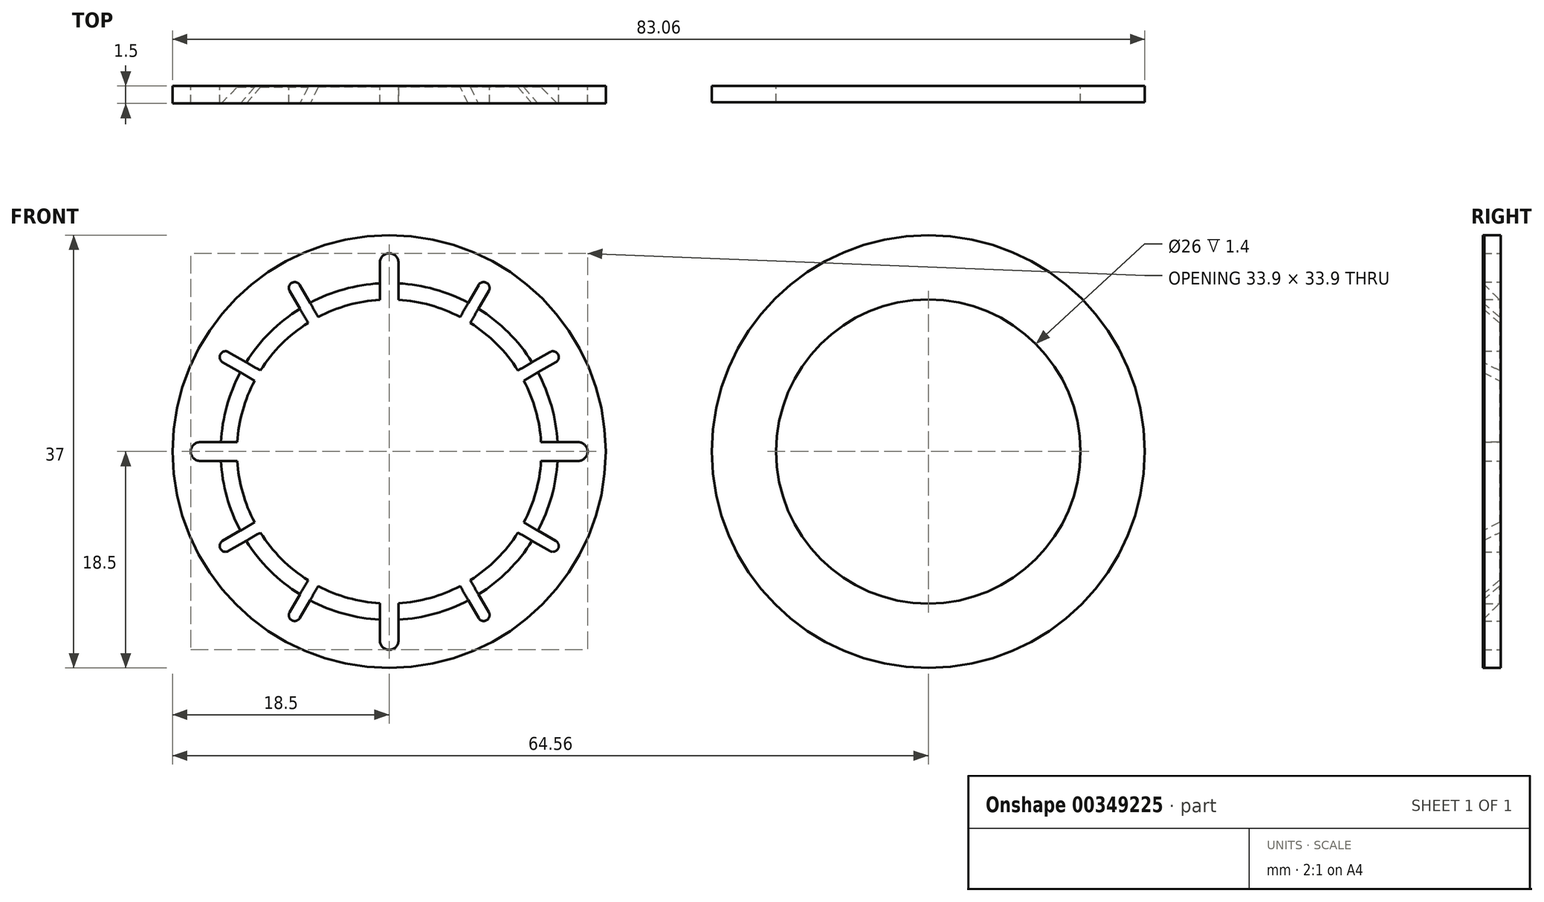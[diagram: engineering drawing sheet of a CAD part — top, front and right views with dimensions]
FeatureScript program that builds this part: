
annotation { "Feature Type Name" : "Feature", "Feature Type Description" : "" }
export const myFeature = defineFeature(function(context is Context, id is Id, definition is map)
    precondition{}
    {
        {
            var Q0;
            Q0=qCreatedBy(makeId("Front.planeOp"),FACE);
            var sketch = newSketch(context, id + "F0", { "sketchPlane" : qUnion([Q0])});
            skCircle(sketch, "E0", {"center": v(0, 0) * mm, "radius": 18.5 * mm});
            skCircle(sketch, "E1", {"center": v(0, 0) * mm, "radius": 13 * mm});
            skCircle(sketch, "E2", {"center": v(-16.15, 0) * mm, "radius": 0.5 * mm});
            skLineSegment(sketch, "E3", {"start": v(-16.15, 0.5) * mm, "end": v(-13, 0.5) * mm});
            skLineSegment(sketch, "E4.MirrorCS", {"start": v(-16.15, -0.5) * mm, "end": v(-13, -0.5) * mm});
            skCircle(sketch, "E5.1.0", {"center": v(-13.99, -8.07) * mm, "radius": 0.5 * mm});
            skLineSegment(sketch, "E5.1.1", {"start": v(-13.74, -8.5) * mm, "end": v(-11, -6.93) * mm});
            skLineSegment(sketch, "E5.1.2", {"start": v(-14.24, -7.64) * mm, "end": v(-11.5, -6.06) * mm});
            skCircle(sketch, "E5.2.0", {"center": v(-8.08, -13.99) * mm, "radius": 0.5 * mm});
            skLineSegment(sketch, "E5.2.1", {"start": v(-7.64, -14.24) * mm, "end": v(-6.06, -11.5) * mm});
            skLineSegment(sketch, "E5.2.2", {"start": v(-8.5, -13.74) * mm, "end": v(-6.93, -11) * mm});
            skCircle(sketch, "E6.1.3.0", {"center": v(0, -16.15) * mm, "radius": 0.5 * mm});
            skLineSegment(sketch, "E6.2.3.0", {"start": v(0.5, -16.15) * mm, "end": v(0.5, -13) * mm});
            skLineSegment(sketch, "E6.5.3.0", {"start": v(-0.5, -16.15) * mm, "end": v(-0.5, -13) * mm});
            skCircle(sketch, "E6.1.4.0", {"center": v(8.07, -13.99) * mm, "radius": 0.5 * mm});
            skLineSegment(sketch, "E6.2.4.0", {"start": v(8.5, -13.74) * mm, "end": v(6.93, -11) * mm});
            skLineSegment(sketch, "E6.5.4.0", {"start": v(7.64, -14.24) * mm, "end": v(6.06, -11.5) * mm});
            skCircle(sketch, "E6.1.5.0", {"center": v(13.99, -8.07) * mm, "radius": 0.5 * mm});
            skLineSegment(sketch, "E6.2.5.0", {"start": v(14.24, -7.64) * mm, "end": v(11.5, -6.06) * mm});
            skLineSegment(sketch, "E6.5.5.0", {"start": v(13.74, -8.5) * mm, "end": v(11, -6.93) * mm});
            skCircle(sketch, "E6.1.6.0", {"center": v(16.15, 0) * mm, "radius": 0.5 * mm});
            skLineSegment(sketch, "E6.2.6.0", {"start": v(16.15, 0.5) * mm, "end": v(13, 0.5) * mm});
            skLineSegment(sketch, "E6.5.6.0", {"start": v(16.15, -0.5) * mm, "end": v(13, -0.5) * mm});
            skCircle(sketch, "E6.1.7.0", {"center": v(13.99, 8.07) * mm, "radius": 0.5 * mm});
            skLineSegment(sketch, "E6.2.7.0", {"start": v(13.74, 8.5) * mm, "end": v(11, 6.93) * mm});
            skLineSegment(sketch, "E6.5.7.0", {"start": v(14.24, 7.64) * mm, "end": v(11.5, 6.06) * mm});
            skCircle(sketch, "E6.1.8.0", {"center": v(8.08, 13.99) * mm, "radius": 0.5 * mm});
            skLineSegment(sketch, "E6.2.8.0", {"start": v(7.64, 14.24) * mm, "end": v(6.06, 11.5) * mm});
            skLineSegment(sketch, "E6.5.8.0", {"start": v(8.5, 13.74) * mm, "end": v(6.93, 11) * mm});
            skCircle(sketch, "E6.1.9.0", {"center": v(0, 16.15) * mm, "radius": 0.5 * mm});
            skLineSegment(sketch, "E6.2.9.0", {"start": v(-0.5, 16.15) * mm, "end": v(-0.5, 13) * mm});
            skLineSegment(sketch, "E6.5.9.0", {"start": v(0.5, 16.15) * mm, "end": v(0.5, 13) * mm});
            skCircle(sketch, "E6.1.10.0", {"center": v(-8.08, 13.99) * mm, "radius": 0.5 * mm});
            skLineSegment(sketch, "E6.2.10.0", {"start": v(-8.5, 13.74) * mm, "end": v(-6.93, 11) * mm});
            skLineSegment(sketch, "E6.5.10.0", {"start": v(-7.64, 14.24) * mm, "end": v(-6.06, 11.5) * mm});
            skCircle(sketch, "E6.1.11.0", {"center": v(-13.99, 8.08) * mm, "radius": 0.5 * mm});
            skLineSegment(sketch, "E6.2.11.0", {"start": v(-14.24, 7.64) * mm, "end": v(-11.5, 6.06) * mm});
            skLineSegment(sketch, "E6.5.11.0", {"start": v(-13.74, 8.5) * mm, "end": v(-11, 6.93) * mm});
            skCircle(sketch, "E7", {"center": v(-16.15, 0) * mm, "radius": 0.8 * mm});
            skLineSegment(sketch, "E8", {"start": v(-16.15, 0.8) * mm, "end": v(-12.98, 0.8) * mm});
            skLineSegment(sketch, "E9.MirrorCS", {"start": v(-16.15, -0.8) * mm, "end": v(-12.98, -0.8) * mm});
            skCircle(sketch, "E10.1.0", {"center": v(0, -16.15) * mm, "radius": 0.8 * mm});
            skLineSegment(sketch, "E10.1.1", {"start": v(-0.8, -16.15) * mm, "end": v(-0.8, -12.98) * mm});
            skLineSegment(sketch, "E10.1.2", {"start": v(0.8, -16.15) * mm, "end": v(0.8, -12.98) * mm});
            skCircle(sketch, "E10.2.0", {"center": v(16.15, 0) * mm, "radius": 0.8 * mm});
            skLineSegment(sketch, "E10.2.1", {"start": v(16.15, -0.8) * mm, "end": v(12.98, -0.8) * mm});
            skLineSegment(sketch, "E10.2.2", {"start": v(16.15, 0.8) * mm, "end": v(12.98, 0.8) * mm});
            skCircle(sketch, "E11.1.3.0", {"center": v(0, 16.15) * mm, "radius": 0.8 * mm});
            skLineSegment(sketch, "E11.2.3.0", {"start": v(0.8, 16.15) * mm, "end": v(0.8, 12.98) * mm});
            skLineSegment(sketch, "E11.5.3.0", {"start": v(-0.8, 16.15) * mm, "end": v(-0.8, 12.98) * mm});
            skCircle(sketch, "E12", {"center": v(46.06, 0) * mm, "radius": 18.5 * mm});
            skCircle(sketch, "E13", {"center": v(46.06, 0) * mm, "radius": 13 * mm});
            skSolve(sketch);
        }
        {
            var Q0;
            {var subQ11=sQuery(id+"F0.wireOp",EDGE,"E6.2.10.0");Q0=makeQuery(id+"F0.imprint","IMPRINT",FACE,{"disambiguationData":[TD([[makeQuery(id+"F0.imprint","IMPRINT",EDGE,{"derivedFrom":subQ11}),-1.0]])]});}
            var Q1;
            {var subQ6=sQuery(id+"F0.wireOp",EDGE,"E5.1.1");Q1=makeQuery(id+"F0.imprint","IMPRINT",FACE,{"disambiguationData":[TD([[makeQuery(id+"F0.imprint","IMPRINT",EDGE,{"derivedFrom":subQ6}),-1.0]])]});}
            extrude(context, id + "F1", {"entities" : qUnion([Q0, Q1]), "offsetDistance" : 25 * mm, "depth" : 1.5 * mm});
        }
        {
            var Q0;
            {var subQ0=sQuery(id+"F0.wireOp",EDGE,"E1");Q0=makeQuery(id+"F1.opExtrude","CAP_EDGE",EDGE,{"disambiguationData":[OSD([subQ0]),TDD([makeQuery(id+"F0.imprint","IMPRINT",EDGE,{"disambiguationData":[TD([[makeQuery(id+"F0.imprint","INTERSECT",VERTEX,{"derivedFrom":[subQ0,sQuery(id+"F0.wireOp",EDGE,"E6.2.11.0")]}),-1.0]])],"derivedFrom":subQ0})])],"isStart":false});}
            var Q1;
            {var subQ0=sQuery(id+"F0.wireOp",EDGE,"E1");Q1=makeQuery(id+"F1.opExtrude","CAP_EDGE",EDGE,{"disambiguationData":[OSD([subQ0]),TDD([makeQuery(id+"F0.imprint","IMPRINT",EDGE,{"disambiguationData":[TD([[makeQuery(id+"F0.imprint","INTERSECT",VERTEX,{"derivedFrom":[subQ0,sQuery(id+"F0.wireOp",EDGE,"E6.2.10.0")]}),-1.0]])],"derivedFrom":subQ0})])],"isStart":false});}
            var Q2;
            {var subQ0=sQuery(id+"F0.wireOp",EDGE,"E1");Q2=makeQuery(id+"F1.opExtrude","CAP_EDGE",EDGE,{"disambiguationData":[OSD([subQ0]),TDD([makeQuery(id+"F0.imprint","IMPRINT",EDGE,{"disambiguationData":[TD([[makeQuery(id+"F0.imprint","INTERSECT",VERTEX,{"derivedFrom":[subQ0,sQuery(id+"F0.wireOp",EDGE,"E6.5.10.0")]}),1.0]])],"derivedFrom":subQ0})])],"isStart":false});}
            var Q3;
            {var subQ0=sQuery(id+"F0.wireOp",EDGE,"E1");Q3=makeQuery(id+"F1.opExtrude","CAP_EDGE",EDGE,{"disambiguationData":[OSD([subQ0]),TDD([makeQuery(id+"F0.imprint","IMPRINT",EDGE,{"disambiguationData":[TD([[makeQuery(id+"F0.imprint","INTERSECT",VERTEX,{"derivedFrom":[subQ0,sQuery(id+"F0.wireOp",EDGE,"E6.2.8.0")]}),-1.0]])],"derivedFrom":subQ0})])],"isStart":false});}
            var Q4;
            {var subQ0=sQuery(id+"F0.wireOp",EDGE,"E1");Q4=makeQuery(id+"F1.opExtrude","CAP_EDGE",EDGE,{"disambiguationData":[OSD([subQ0]),TDD([makeQuery(id+"F0.imprint","IMPRINT",EDGE,{"disambiguationData":[TD([[makeQuery(id+"F0.imprint","INTERSECT",VERTEX,{"derivedFrom":[subQ0,sQuery(id+"F0.wireOp",EDGE,"E6.2.7.0")]}),-1.0]])],"derivedFrom":subQ0})])],"isStart":false});}
            var Q5;
            {var subQ0=sQuery(id+"F0.wireOp",EDGE,"E1");Q5=makeQuery(id+"F1.opExtrude","CAP_EDGE",EDGE,{"disambiguationData":[OSD([subQ0]),TDD([makeQuery(id+"F0.imprint","IMPRINT",EDGE,{"disambiguationData":[TD([[makeQuery(id+"F0.imprint","INTERSECT",VERTEX,{"derivedFrom":[subQ0,sQuery(id+"F0.wireOp",EDGE,"E6.5.7.0")]}),1.0]])],"derivedFrom":subQ0})])],"isStart":false});}
            var Q6;
            {var subQ0=sQuery(id+"F0.wireOp",EDGE,"E1");Q6=makeQuery(id+"F1.opExtrude","CAP_EDGE",EDGE,{"disambiguationData":[OSD([subQ0]),TDD([makeQuery(id+"F0.imprint","IMPRINT",EDGE,{"disambiguationData":[TD([[makeQuery(id+"F0.imprint","INTERSECT",VERTEX,{"derivedFrom":[subQ0,sQuery(id+"F0.wireOp",EDGE,"E6.2.5.0")]}),-1.0]])],"derivedFrom":subQ0})])],"isStart":false});}
            var Q7;
            {var subQ0=sQuery(id+"F0.wireOp",EDGE,"E1");Q7=makeQuery(id+"F1.opExtrude","CAP_EDGE",EDGE,{"disambiguationData":[OSD([subQ0]),TDD([makeQuery(id+"F0.imprint","IMPRINT",EDGE,{"disambiguationData":[TD([[makeQuery(id+"F0.imprint","INTERSECT",VERTEX,{"derivedFrom":[subQ0,sQuery(id+"F0.wireOp",EDGE,"E6.2.4.0")]}),-1.0]])],"derivedFrom":subQ0})])],"isStart":false});}
            var Q8;
            {var subQ0=sQuery(id+"F0.wireOp",EDGE,"E1");Q8=makeQuery(id+"F1.opExtrude","CAP_EDGE",EDGE,{"disambiguationData":[OSD([subQ0]),TDD([makeQuery(id+"F0.imprint","IMPRINT",EDGE,{"disambiguationData":[TD([[makeQuery(id+"F0.imprint","INTERSECT",VERTEX,{"derivedFrom":[subQ0,sQuery(id+"F0.wireOp",EDGE,"E6.5.4.0")]}),1.0]])],"derivedFrom":subQ0})])],"isStart":false});}
            var Q9;
            {var subQ0=sQuery(id+"F0.wireOp",EDGE,"E1");Q9=makeQuery(id+"F1.opExtrude","CAP_EDGE",EDGE,{"disambiguationData":[OSD([subQ0]),TDD([makeQuery(id+"F0.imprint","IMPRINT",EDGE,{"disambiguationData":[TD([[makeQuery(id+"F0.imprint","INTERSECT",VERTEX,{"derivedFrom":[subQ0,sQuery(id+"F0.wireOp",EDGE,"E5.2.1")]}),-1.0]])],"derivedFrom":subQ0})])],"isStart":false});}
            var Q10;
            {var subQ0=sQuery(id+"F0.wireOp",EDGE,"E1");Q10=makeQuery(id+"F1.opExtrude","CAP_EDGE",EDGE,{"disambiguationData":[OSD([subQ0]),TDD([makeQuery(id+"F0.imprint","IMPRINT",EDGE,{"disambiguationData":[TD([[makeQuery(id+"F0.imprint","INTERSECT",VERTEX,{"derivedFrom":[subQ0,sQuery(id+"F0.wireOp",EDGE,"E5.1.1")]}),-1.0]])],"derivedFrom":subQ0})])],"isStart":false});}
            var Q11;
            {var subQ0=sQuery(id+"F0.wireOp",EDGE,"E1");Q11=makeQuery(id+"F1.opExtrude","CAP_EDGE",EDGE,{"disambiguationData":[OSD([subQ0]),TDD([makeQuery(id+"F0.imprint","IMPRINT",EDGE,{"disambiguationData":[TD([[makeQuery(id+"F0.imprint","INTERSECT",VERTEX,{"derivedFrom":[subQ0,sQuery(id+"F0.wireOp",EDGE,"E5.1.2")]}),1.0]])],"derivedFrom":subQ0})])],"isStart":false});}
            chamfer(context, id + "F2", {"entities" : qUnion([Q0, Q1, Q2, Q3, Q4, Q5, Q6, Q7, Q8, Q9, Q10, Q11]), "width" : 1.4 * mm, "tangentPropagation" : true});
        }
        {
            var Q0;
            Q0=makeQuery(id+"F0.imprint","IMPRINT",FACE,{"disambiguationData":[TD([[makeQuery(id+"F0.imprint","IMPRINT",EDGE,{"derivedFrom":sQuery(id+"F0.wireOp",EDGE,"E12")}),1.0]])]});
            extrude(context, id + "F3", {"entities" : qUnion([Q0]), "offsetDistance" : 25 * mm, "depth" : 1.4 * mm});
        }
    });
